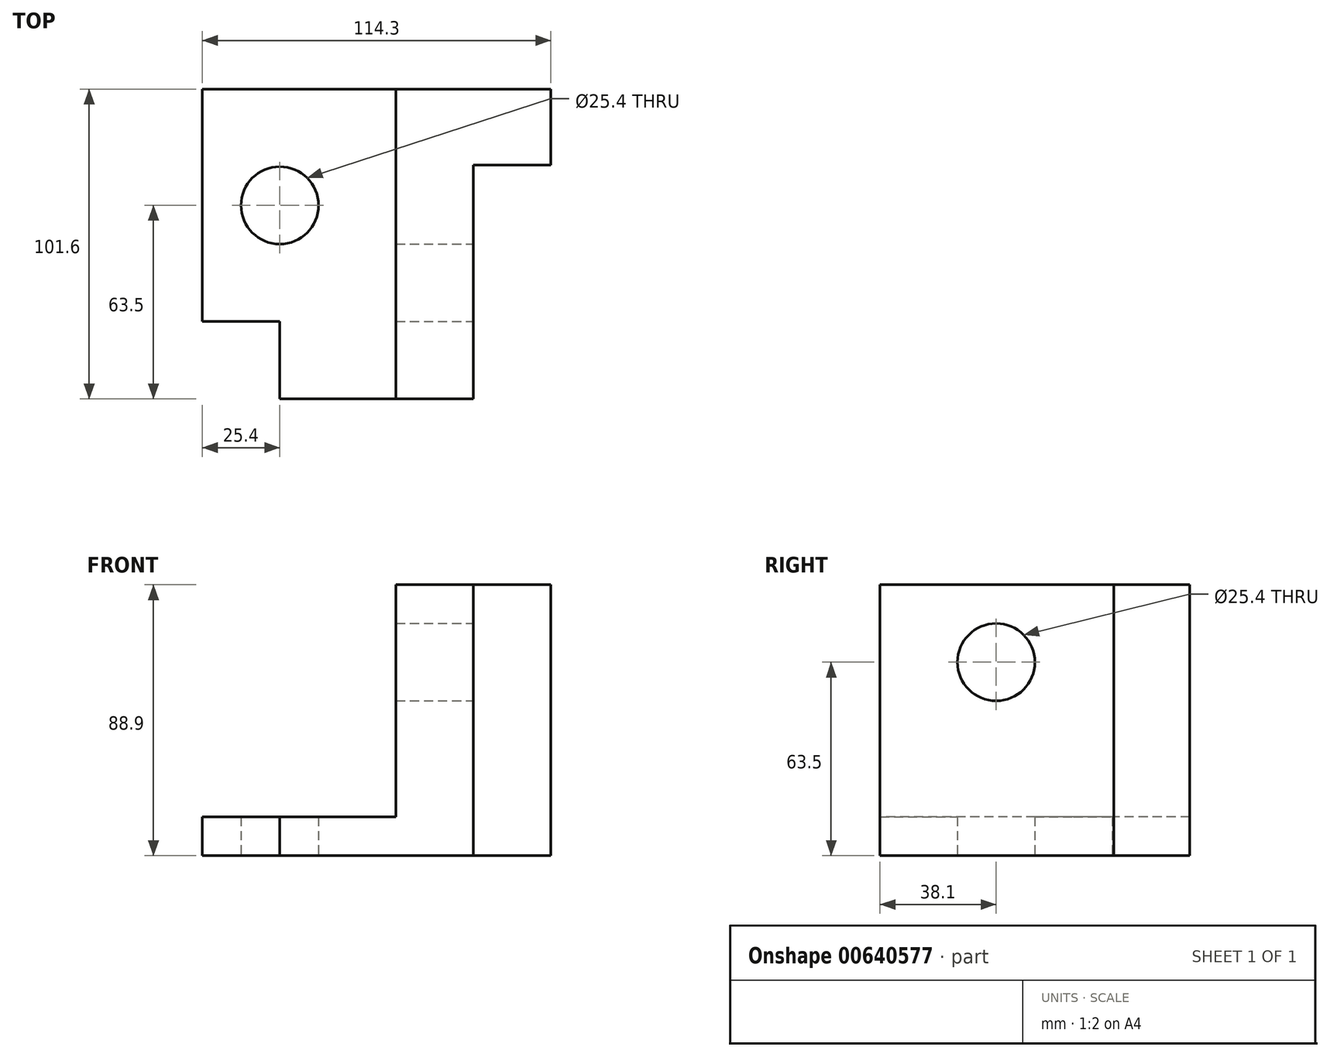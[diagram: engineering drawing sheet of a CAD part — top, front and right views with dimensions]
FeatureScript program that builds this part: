
annotation { "Feature Type Name" : "Feature", "Feature Type Description" : "" }
export const myFeature = defineFeature(function(context is Context, id is Id, definition is map)
    precondition{}
    {
        {
            var Q0;
            Q0=qCreatedBy(makeId("Top.planeOp"),FACE);
            var sketch = newSketch(context, id + "F0", { "sketchPlane" : qUnion([Q0])});
            skLineSegment(sketch, "E0.bottom", {"start": v(38.1, -50.8) * mm, "end": v(-38.1, -50.8) * mm});
            skLineSegment(sketch, "E0.top", {"start": v(38.1, 50.8) * mm, "end": v(-38.1, 50.8) * mm});
            skLineSegment(sketch, "E0.left", {"start": v(38.1, -50.8) * mm, "end": v(38.1, 50.8) * mm});
            skLineSegment(sketch, "E0.right", {"start": v(-38.1, -50.8) * mm, "end": v(-38.1, -25.4) * mm});
            skPoint(sketch, "E0.middle", {"position": v(0, 0) * mm});
            skLineSegment(sketch, "E1", {"start": v(-38.1, 50.8) * mm, "end": v(-63.5, 50.8) * mm});
            skLineSegment(sketch, "E2", {"start": v(-63.5, 50.8) * mm, "end": v(-63.5, -25.4) * mm});
            skLineSegment(sketch, "E3", {"start": v(-63.5, -25.4) * mm, "end": v(-38.1, -25.4) * mm});
            skCircle(sketch, "E4", {"center": v(-38.1, 12.7) * mm, "radius": 12.7 * mm});
            skSolve(sketch);
        }
        {
            var Q0;
            Q0 = qSketchRegion(id + "F0", true);
            extrude(context, id + "F1", {"entities" : qUnion([Q0]), "depth" : 12.7 * mm, "offsetDistance" : 25.4 * mm});
        }
        {
            var Q0;
            Q0=makeQuery(id+"F1.opExtrude","CAP_FACE",FACE,{"disambiguationData":[OSD([sQuery(id+"F0.wireOp",EDGE,"E0.bottom"),sQuery(id+"F0.wireOp",EDGE,"E0.top"),sQuery(id+"F0.wireOp",EDGE,"E0.left"),sQuery(id+"F0.wireOp",EDGE,"E0.right"),sQuery(id+"F0.wireOp",EDGE,"E1"),sQuery(id+"F0.wireOp",EDGE,"E2"),sQuery(id+"F0.wireOp",EDGE,"E3"),sQuery(id+"F0.wireOp",EDGE,"E4")])],"isStart":false});
            var sketch = newSketch(context, id + "F2", { "sketchPlane" : qUnion([Q0])});
            skLineSegment(sketch, "E5.bottom", {"start": v(0, 50.8) * mm, "end": v(25.4, 50.8) * mm});
            skLineSegment(sketch, "E5.top", {"start": v(0, -50.8) * mm, "end": v(25.4, -50.8) * mm});
            skLineSegment(sketch, "E5.left", {"start": v(0, 50.8) * mm, "end": v(0, -50.8) * mm});
            skLineSegment(sketch, "E5.right", {"start": v(25.4, 50.8) * mm, "end": v(25.4, -50.8) * mm});
            skSolve(sketch);
        }
        {
            var Q0;
            {var subQ0=sQuery(id+"F2.wireOp",EDGE,"E5.right");Q0=makeQuery(id+"F2.imprint","IMPRINT",FACE,{"disambiguationData":[TD([[makeQuery(id+"F2.imprint","IMPRINT",EDGE,{"derivedFrom":subQ0}),1.0]])]});}
            extrude(context, id + "F3", {"entities" : qUnion([Q0]), "operationType" : NewBodyOperationType.REMOVE, "oppositeDirection" : true, "depth" : 25.4 * mm, "offsetDistance" : 25.4 * mm});
        }
        {
            var Q0;
            Q0=makeQuery(id+"F2.imprint","IMPRINT",FACE,{"disambiguationData":[TD([[makeQuery(id+"F2.imprint","IMPRINT",EDGE,{"derivedFrom":sQuery(id+"F2.wireOp",EDGE,"E5.bottom")}),1.0]])]});
            extrude(context, id + "F4", {"entities" : qUnion([Q0]), "operationType" : NewBodyOperationType.ADD, "depth" : 76.2 * mm, "offsetDistance" : 25.4 * mm});
        }
        {
            var Q0;
            {var subQ0=sQuery(id+"F2.wireOp",EDGE,"E5.right");Q0=makeQuery(id+"F4.boolean.opBoolean","MERGE",FACE,{"derivedFrom":[makeQuery(id+"F3.boolean.opBoolean","COPY",FACE,{"derivedFrom":makeQuery(id+"F3.opExtrude","SWEPT_FACE",FACE,{"disambiguationData":[OSD([subQ0])]})}),makeQuery(id+"F4.opExtrude","SWEPT_FACE",FACE,{"disambiguationData":[OSD([subQ0])]})]});}
            var sketch = newSketch(context, id + "F5", { "sketchPlane" : qUnion([Q0])});
            skCircle(sketch, "E6", {"center": v(-12.7, 63.5) * mm, "radius": 12.7 * mm});
            skSolve(sketch);
        }
        {
            var Q0;
            Q0=makeQuery(id+"F5.imprint","IMPRINT",FACE,{"disambiguationData":[TD([[makeQuery(id+"F5.imprint","IMPRINT",EDGE,{"derivedFrom":sQuery(id+"F5.wireOp",EDGE,"E6")}),1.0]])]});
            extrude(context, id + "F6", {"entities" : qUnion([Q0]), "operationType" : NewBodyOperationType.REMOVE, "oppositeDirection" : true, "depth" : 25.4 * mm, "offsetDistance" : 25.4 * mm});
        }
        {
            var Q0;
            {var subQ0=sQuery(id+"F2.wireOp",EDGE,"E5.right");Q0=makeQuery(id+"F4.boolean.opBoolean","MERGE",FACE,{"derivedFrom":[makeQuery(id+"F3.boolean.opBoolean","COPY",FACE,{"derivedFrom":makeQuery(id+"F3.opExtrude","SWEPT_FACE",FACE,{"disambiguationData":[OSD([subQ0])]})}),makeQuery(id+"F4.opExtrude","SWEPT_FACE",FACE,{"disambiguationData":[OSD([subQ0])]})]});}
            var sketch = newSketch(context, id + "F7", { "sketchPlane" : qUnion([Q0])});
            skLineSegment(sketch, "E7", {"start": v(50.8, 88.9) * mm, "end": v(25.91, 88.9) * mm});
            skLineSegment(sketch, "E8", {"start": v(25.91, 88.9) * mm, "end": v(25.91, 0) * mm});
            skLineSegment(sketch, "E9", {"start": v(25.91, 0) * mm, "end": v(50.8, 0) * mm});
            skLineSegment(sketch, "E10", {"start": v(50.8, 0) * mm, "end": v(50.8, 88.9) * mm});
            skSolve(sketch);
        }
        {
            var Q0;
            Q0=makeQuery(id+"F7.imprint","IMPRINT",FACE,{"disambiguationData":[TD([[makeQuery(id+"F7.imprint","IMPRINT",EDGE,{"derivedFrom":sQuery(id+"F7.wireOp",EDGE,"E7")}),1.0]])]});
            extrude(context, id + "F8", {"entities" : qUnion([Q0]), "operationType" : NewBodyOperationType.ADD, "depth" : 25.4 * mm, "offsetDistance" : 25.4 * mm});
        }
    });
